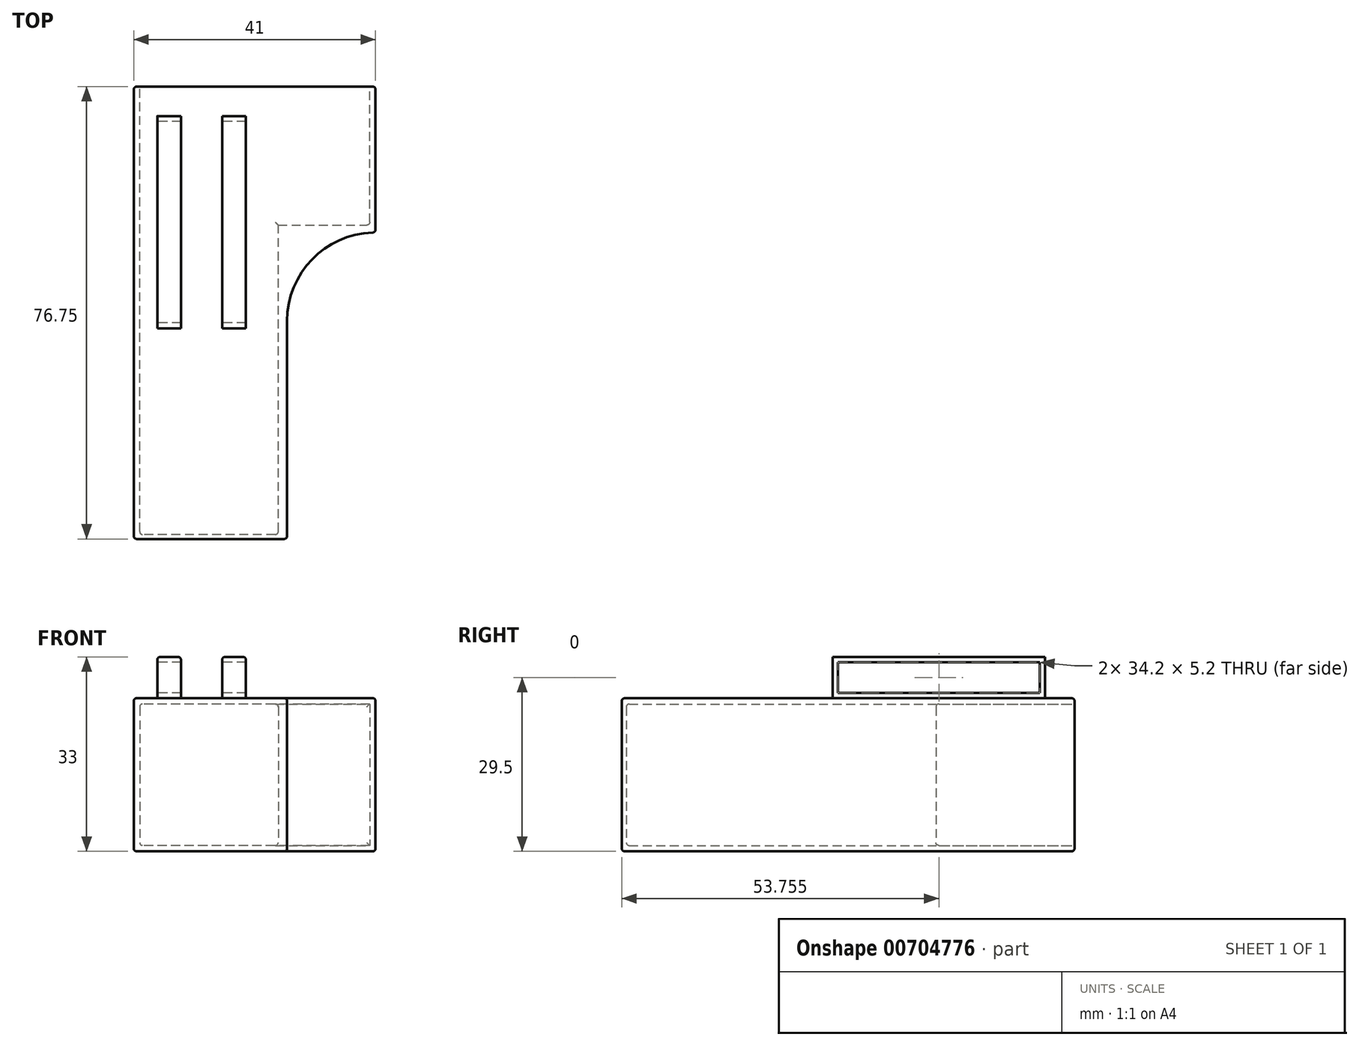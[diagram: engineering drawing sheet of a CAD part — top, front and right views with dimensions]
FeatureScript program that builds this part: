
annotation { "Feature Type Name" : "Feature", "Feature Type Description" : "" }
export const myFeature = defineFeature(function(context is Context, id is Id, definition is map)
    precondition{}
    {
        {
            var Q0;
            Q0=qCreatedBy(makeId("Top.planeOp"),FACE);
            var sketch = newSketch(context, id + "F0", { "sketchPlane" : qUnion([Q0])});
            skLineSegment(sketch, "E0", {"start": v(11.6, -39.6) * mm, "end": v(-14.4, -39.6) * mm});
            skLineSegment(sketch, "E1", {"start": v(-14.4, -39.6) * mm, "end": v(-14.4, 37.14) * mm});
            skLineSegment(sketch, "E2", {"start": v(-14.4, 37.14) * mm, "end": v(26.6, 37.14) * mm});
            skLineSegment(sketch, "E3", {"start": v(26.6, 37.14) * mm, "end": v(26.6, 12.4) * mm});
            skLineSegment(sketch, "E4", {"start": v(26.6, 12.4) * mm, "end": v(11.6, 12.4) * mm});
            skLineSegment(sketch, "E5", {"start": v(11.6, 12.4) * mm, "end": v(11.6, -39.6) * mm});
            skSolve(sketch);
        }
        {
            var Q0;
            Q0=makeQuery(id+"F0.imprint","IMPRINT",FACE,{"disambiguationData":[TD([[makeQuery(id+"F0.imprint","IMPRINT",EDGE,{"derivedFrom":sQuery(id+"F0.wireOp",EDGE,"E0")}),-1.0]])]});
            extrude(context, id + "F1", {"entities" : qUnion([Q0]), "endBound" : BoundingType.SYMMETRIC, "depth" : 26 * mm, "offsetDistance" : 25 * mm});
        }
        {
            var Q0;
            Q0=makeQuery(id+"F1.opExtrude","SWEPT_FACE",FACE,{"disambiguationData":[OSD([sQuery(id+"F0.wireOp",EDGE,"E2")])]});
            var sketch = newSketch(context, id + "F2", { "sketchPlane" : qUnion([Q0])});
            skLineSegment(sketch, "E6.bottom", {"start": v(-10.1, 12) * mm, "end": v(13.4, 12) * mm});
            skLineSegment(sketch, "E6.top", {"start": v(-10.1, -12) * mm, "end": v(13.4, -12) * mm});
            skLineSegment(sketch, "E6.left", {"start": v(-10.1, 12) * mm, "end": v(-10.1, -12) * mm});
            skLineSegment(sketch, "E6.right", {"start": v(13.4, 12) * mm, "end": v(13.4, -12) * mm});
            skSolve(sketch);
        }
        {
            var Q0;
            Q0=makeQuery(id+"F2.imprint","IMPRINT",FACE,{"disambiguationData":[TD([[makeQuery(id+"F2.imprint","IMPRINT",EDGE,{"derivedFrom":sQuery(id+"F2.wireOp",EDGE,"E6.bottom")}),-1.0]])]});
            extrude(context, id + "F3", {"entities" : qUnion([Q0]), "operationType" : NewBodyOperationType.REMOVE, "oppositeDirection" : true, "depth" : 76 * mm, "offsetDistance" : 25 * mm});
        }
        {
            var Q0;
            Q0=makeQuery(id+"F1.opExtrude","SWEPT_FACE",FACE,{"disambiguationData":[OSD([sQuery(id+"F0.wireOp",EDGE,"E2")])]});
            var sketch = newSketch(context, id + "F4", { "sketchPlane" : qUnion([Q0])});
            skLineSegment(sketch, "E7.bottom", {"start": v(-10.1, 12) * mm, "end": v(-25.6, 12) * mm});
            skLineSegment(sketch, "E7.top", {"start": v(-10.1, -12) * mm, "end": v(-25.6, -12) * mm});
            skLineSegment(sketch, "E7.left", {"start": v(-10.1, 12) * mm, "end": v(-10.1, -12) * mm});
            skLineSegment(sketch, "E7.right", {"start": v(-25.6, 12) * mm, "end": v(-25.6, -12) * mm});
            skSolve(sketch);
        }
        {
            var Q0;
            Q0=makeQuery(id+"F4.imprint","IMPRINT",FACE,{"disambiguationData":[TD([[makeQuery(id+"F4.imprint","IMPRINT",EDGE,{"derivedFrom":sQuery(id+"F4.wireOp",EDGE,"E7.bottom")}),1.0]])]});
            extrude(context, id + "F5", {"entities" : qUnion([Q0]), "operationType" : NewBodyOperationType.REMOVE, "oppositeDirection" : true, "depth" : 23.5 * mm, "offsetDistance" : 25 * mm});
        }
        {
            var Q0;
            Q0=makeQuery(id+"F1.opExtrude","CAP_FACE",FACE,{"disambiguationData":[OSD([sQuery(id+"F0.wireOp",EDGE,"E0"),sQuery(id+"F0.wireOp",EDGE,"E1"),sQuery(id+"F0.wireOp",EDGE,"E2"),sQuery(id+"F0.wireOp",EDGE,"E3"),sQuery(id+"F0.wireOp",EDGE,"E4"),sQuery(id+"F0.wireOp",EDGE,"E5")])],"isStart":false});
            var sketch = newSketch(context, id + "F6", { "sketchPlane" : qUnion([Q0])});
            skLineSegment(sketch, "E8.bottom", {"start": v(-10.4, 32.14) * mm, "end": v(-6.4, 32.14) * mm});
            skLineSegment(sketch, "E8.top", {"start": v(-10.4, -3.86) * mm, "end": v(-6.4, -3.86) * mm});
            skLineSegment(sketch, "E8.left", {"start": v(-10.4, 32.14) * mm, "end": v(-10.4, -3.86) * mm});
            skLineSegment(sketch, "E8.right", {"start": v(-6.4, 32.14) * mm, "end": v(-6.4, -3.86) * mm});
            skLineSegment(sketch, "E9.bottom", {"start": v(4.6, -3.86) * mm, "end": v(0.6, -3.86) * mm});
            skLineSegment(sketch, "E9.top", {"start": v(4.6, 32.14) * mm, "end": v(0.6, 32.14) * mm});
            skLineSegment(sketch, "E9.left", {"start": v(4.6, -3.86) * mm, "end": v(4.6, 32.14) * mm});
            skLineSegment(sketch, "E9.right", {"start": v(0.6, -3.86) * mm, "end": v(0.6, 32.14) * mm});
            skSolve(sketch);
        }
        {
            var Q0;
            Q0=makeQuery(id+"F6.imprint","IMPRINT",FACE,{"disambiguationData":[TD([[makeQuery(id+"F6.imprint","IMPRINT",EDGE,{"derivedFrom":sQuery(id+"F6.wireOp",EDGE,"E8.bottom")}),-1.0]])]});
            var Q1;
            Q1=makeQuery(id+"F6.imprint","IMPRINT",FACE,{"disambiguationData":[TD([[makeQuery(id+"F6.imprint","IMPRINT",EDGE,{"derivedFrom":sQuery(id+"F6.wireOp",EDGE,"E9.bottom")}),-1.0]])]});
            extrude(context, id + "F7", {"entities" : qUnion([Q0, Q1]), "operationType" : NewBodyOperationType.ADD, "depth" : 7 * mm, "offsetDistance" : 25 * mm});
        }
        {
            var Q0;
            Q0=makeQuery(id+"F7.opExtrude","SWEPT_FACE",FACE,{"disambiguationData":[OSD([sQuery(id+"F6.wireOp",EDGE,"E8.left")])]});
            var sketch = newSketch(context, id + "F8", { "sketchPlane" : qUnion([Q0])});
            skLineSegment(sketch, "E10.bottom", {"start": v(-31.24, 19.1) * mm, "end": v(2.96, 19.1) * mm});
            skLineSegment(sketch, "E10.top", {"start": v(-31.24, 13.9) * mm, "end": v(2.96, 13.9) * mm});
            skLineSegment(sketch, "E10.left", {"start": v(-31.24, 19.1) * mm, "end": v(-31.24, 13.9) * mm});
            skLineSegment(sketch, "E10.right", {"start": v(2.96, 19.1) * mm, "end": v(2.96, 13.9) * mm});
            skSolve(sketch);
        }
        {
            var Q0;
            Q0=makeQuery(id+"F8.imprint","IMPRINT",FACE,{"disambiguationData":[TD([[makeQuery(id+"F8.imprint","IMPRINT",EDGE,{"derivedFrom":sQuery(id+"F8.wireOp",EDGE,"E10.bottom")}),-1.0]])]});
            extrude(context, id + "F9", {"entities" : qUnion([Q0]), "operationType" : NewBodyOperationType.REMOVE, "oppositeDirection" : true, "depth" : 25 * mm, "offsetDistance" : 25 * mm});
        }
        {
            var Q0;
            Q0=makeQuery(id+"F1.opExtrude","SWEPT_EDGE",EDGE,{"disambiguationData":[OSD([sQuery(id+"F0.wireOp",EDGE,"E4"),sQuery(id+"F0.wireOp",EDGE,"E5")])]});
            fillet(context, id + "F10", {"entities" : qUnion([Q0]), "radius" : 15 * mm, "tangentPropagation" : true, "allowEdgeOverflow" : false});
        }
        {
            var Q0;
            Q0=makeQuery(id+"F1.opExtrude","CAP_EDGE",EDGE,{"disambiguationData":[OSD([sQuery(id+"F0.wireOp",EDGE,"E5")])],"isStart":false});
            var Q1;
            Q1=makeQuery(id+"F1.opExtrude","CAP_EDGE",EDGE,{"disambiguationData":[OSD([sQuery(id+"F0.wireOp",EDGE,"E5")])],"isStart":true});
            var Q2;
            Q2=makeQuery(id+"F1.opExtrude","CAP_EDGE",EDGE,{"disambiguationData":[OSD([sQuery(id+"F0.wireOp",EDGE,"E1")])],"isStart":false});
            var Q3;
            Q3=makeQuery(id+"F1.opExtrude","CAP_EDGE",EDGE,{"disambiguationData":[OSD([sQuery(id+"F0.wireOp",EDGE,"E1")])],"isStart":true});
            var Q4;
            Q4=makeQuery(id+"F10.opFillet","BLEND_EDGE",EDGE,{"blendedFrom":[makeQuery(id+"F1.opExtrude","SWEPT_EDGE",EDGE,{"disambiguationData":[OSD([sQuery(id+"F0.wireOp",EDGE,"E4"),sQuery(id+"F0.wireOp",EDGE,"E5")])]}),makeQuery(id+"F1.opExtrude","SWEPT_FACE",FACE,{"disambiguationData":[OSD([sQuery(id+"F0.wireOp",EDGE,"E3")])]})],"blendedInto":[makeQuery(id+"F1.opExtrude","SWEPT_FACE",FACE,{"disambiguationData":[OSD([sQuery(id+"F0.wireOp",EDGE,"E3")])]})]});
            var Q5;
            Q5=makeQuery(id+"F1.opExtrude","CAP_EDGE",EDGE,{"disambiguationData":[OSD([sQuery(id+"F0.wireOp",EDGE,"E3")])],"isStart":true});
            var Q6;
            Q6=makeQuery(id+"F1.opExtrude","CAP_EDGE",EDGE,{"disambiguationData":[OSD([sQuery(id+"F0.wireOp",EDGE,"E3")])],"isStart":false});
            var Q7;
            Q7=makeQuery(id+"F1.opExtrude","SWEPT_EDGE",EDGE,{"disambiguationData":[OSD([sQuery(id+"F0.wireOp",EDGE,"E2"),sQuery(id+"F0.wireOp",EDGE,"E3")])]});
            var Q8;
            Q8=makeQuery(id+"F1.opExtrude","CAP_EDGE",EDGE,{"disambiguationData":[OSD([sQuery(id+"F0.wireOp",EDGE,"E2")])],"isStart":false});
            var Q9;
            Q9=makeQuery(id+"F1.opExtrude","CAP_EDGE",EDGE,{"disambiguationData":[OSD([sQuery(id+"F0.wireOp",EDGE,"E2")])],"isStart":true});
            var Q10;
            Q10=makeQuery(id+"F1.opExtrude","SWEPT_EDGE",EDGE,{"disambiguationData":[OSD([sQuery(id+"F0.wireOp",EDGE,"E1"),sQuery(id+"F0.wireOp",EDGE,"E2")])]});
            var Q11;
            Q11=makeQuery(id+"F1.opExtrude","SWEPT_EDGE",EDGE,{"disambiguationData":[OSD([sQuery(id+"F0.wireOp",EDGE,"E0"),sQuery(id+"F0.wireOp",EDGE,"E1")])]});
            var Q12;
            Q12=makeQuery(id+"F1.opExtrude","CAP_EDGE",EDGE,{"disambiguationData":[OSD([sQuery(id+"F0.wireOp",EDGE,"E0")])],"isStart":true});
            var Q13;
            Q13=makeQuery(id+"F1.opExtrude","SWEPT_EDGE",EDGE,{"disambiguationData":[OSD([sQuery(id+"F0.wireOp",EDGE,"E0"),sQuery(id+"F0.wireOp",EDGE,"E5")])]});
            var Q14;
            Q14=makeQuery(id+"F1.opExtrude","CAP_EDGE",EDGE,{"disambiguationData":[OSD([sQuery(id+"F0.wireOp",EDGE,"E0")])],"isStart":false});
            fillet(context, id + "F11", {"entities" : qUnion([Q0, Q1, Q2, Q3, Q4, Q5, Q6, Q7, Q8, Q9, Q10, Q11, Q12, Q13, Q14]), "radius" : 0.5 * mm, "tangentPropagation" : true, "allowEdgeOverflow" : false});
        }
        {
            var Q0;
            Q0=makeQuery(id+"F7.opExtrude","CAP_EDGE",EDGE,{"disambiguationData":[OSD([sQuery(id+"F6.wireOp",EDGE,"E9.left")])],"isStart":false});
            var Q1;
            Q1=makeQuery(id+"F7.opExtrude","CAP_EDGE",EDGE,{"disambiguationData":[OSD([sQuery(id+"F6.wireOp",EDGE,"E9.right")])],"isStart":false});
            var Q2;
            Q2=makeQuery(id+"F7.opExtrude","CAP_EDGE",EDGE,{"disambiguationData":[OSD([sQuery(id+"F6.wireOp",EDGE,"E8.right")])],"isStart":false});
            var Q3;
            Q3=makeQuery(id+"F7.opExtrude","CAP_EDGE",EDGE,{"disambiguationData":[OSD([sQuery(id+"F6.wireOp",EDGE,"E8.left")])],"isStart":false});
            fillet(context, id + "F12", {"entities" : qUnion([Q0, Q1, Q2, Q3]), "radius" : 0.5 * mm, "tangentPropagation" : true, "allowEdgeOverflow" : false});
        }
        {
            var Q0;
            Q0=makeQuery(id+"F3.boolean.opBoolean","COPY",EDGE,{"derivedFrom":makeQuery(id+"F3.opExtrude","SWEPT_EDGE",EDGE,{"disambiguationData":[OSD([sQuery(id+"F2.wireOp",EDGE,"E6.bottom"),sQuery(id+"F2.wireOp",EDGE,"E6.left")])]})});
            var Q1;
            Q1=makeQuery(id+"F3.boolean.opBoolean","COPY",EDGE,{"derivedFrom":makeQuery(id+"F3.opExtrude","SWEPT_EDGE",EDGE,{"disambiguationData":[OSD([sQuery(id+"F2.wireOp",EDGE,"E6.bottom"),sQuery(id+"F2.wireOp",EDGE,"E6.right")])]})});
            var Q2;
            Q2=makeQuery(id+"F3.boolean.opBoolean","COPY",EDGE,{"derivedFrom":makeQuery(id+"F3.opExtrude","SWEPT_EDGE",EDGE,{"disambiguationData":[OSD([sQuery(id+"F2.wireOp",EDGE,"E6.top"),sQuery(id+"F2.wireOp",EDGE,"E6.right")])]})});
            var Q3;
            Q3=makeQuery(id+"F3.boolean.opBoolean","COPY",EDGE,{"derivedFrom":makeQuery(id+"F3.opExtrude","SWEPT_EDGE",EDGE,{"disambiguationData":[OSD([sQuery(id+"F2.wireOp",EDGE,"E6.top"),sQuery(id+"F2.wireOp",EDGE,"E6.left")])]})});
            var Q4;
            Q4=makeQuery(id+"F5.boolean.opBoolean","COPY",EDGE,{"derivedFrom":makeQuery(id+"F5.opExtrude","CAP_EDGE",EDGE,{"disambiguationData":[OSD([sQuery(id+"F4.wireOp",EDGE,"E7.left")])],"isStart":false})});
            var Q5;
            Q5=makeQuery(id+"F5.boolean.opBoolean","COPY",EDGE,{"derivedFrom":makeQuery(id+"F5.opExtrude","CAP_EDGE",EDGE,{"disambiguationData":[OSD([sQuery(id+"F4.wireOp",EDGE,"E7.top")])],"isStart":false})});
            var Q6;
            Q6=makeQuery(id+"F5.boolean.opBoolean","COPY",EDGE,{"derivedFrom":makeQuery(id+"F5.opExtrude","CAP_EDGE",EDGE,{"disambiguationData":[OSD([sQuery(id+"F4.wireOp",EDGE,"E7.bottom")])],"isStart":false})});
            var Q7;
            Q7=makeQuery(id+"F5.boolean.opBoolean","COPY",EDGE,{"derivedFrom":makeQuery(id+"F5.opExtrude","CAP_EDGE",EDGE,{"disambiguationData":[OSD([sQuery(id+"F4.wireOp",EDGE,"E7.right")])],"isStart":false})});
            var Q8;
            Q8=makeQuery(id+"F3.boolean.opBoolean","COPY",EDGE,{"derivedFrom":makeQuery(id+"F3.opExtrude","CAP_EDGE",EDGE,{"disambiguationData":[OSD([sQuery(id+"F2.wireOp",EDGE,"E6.left")])],"isStart":false})});
            var Q9;
            Q9=makeQuery(id+"F3.boolean.opBoolean","COPY",EDGE,{"derivedFrom":makeQuery(id+"F3.opExtrude","CAP_EDGE",EDGE,{"disambiguationData":[OSD([sQuery(id+"F2.wireOp",EDGE,"E6.top")])],"isStart":false})});
            var Q10;
            Q10=makeQuery(id+"F3.boolean.opBoolean","COPY",EDGE,{"derivedFrom":makeQuery(id+"F3.opExtrude","CAP_EDGE",EDGE,{"disambiguationData":[OSD([sQuery(id+"F2.wireOp",EDGE,"E6.right")])],"isStart":false})});
            var Q11;
            Q11=makeQuery(id+"F3.boolean.opBoolean","COPY",EDGE,{"derivedFrom":makeQuery(id+"F3.opExtrude","CAP_EDGE",EDGE,{"disambiguationData":[OSD([sQuery(id+"F2.wireOp",EDGE,"E6.bottom")])],"isStart":false})});
            fillet(context, id + "F13", {"entities" : qUnion([Q0, Q1, Q2, Q3, Q4, Q5, Q6, Q7, Q8, Q9, Q10, Q11]), "radius" : 0.5 * mm, "tangentPropagation" : true, "allowEdgeOverflow" : false});
        }
    });
